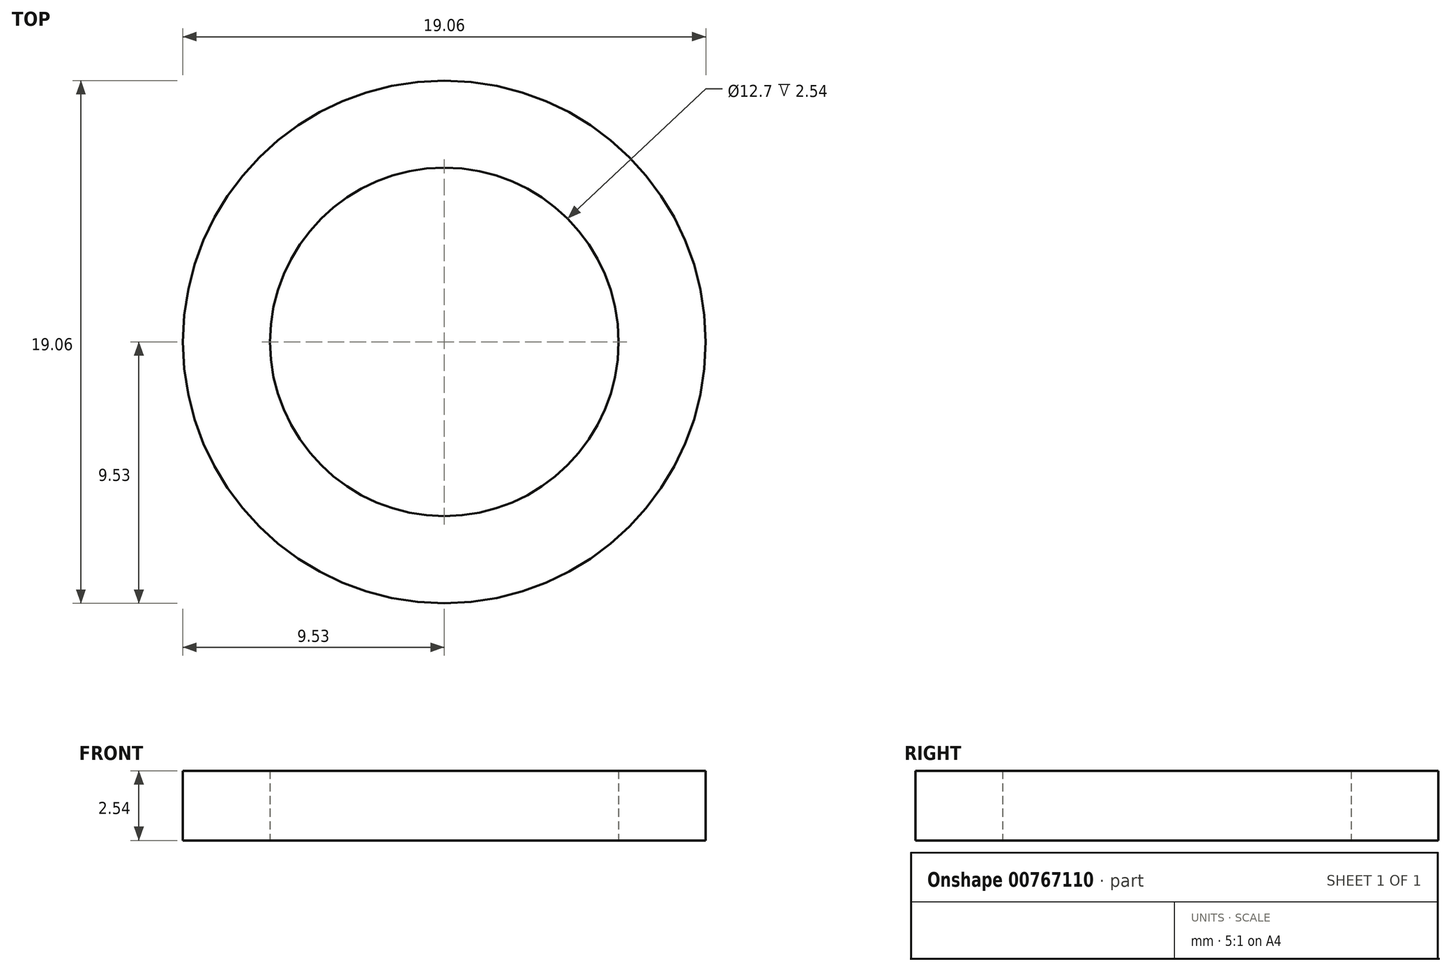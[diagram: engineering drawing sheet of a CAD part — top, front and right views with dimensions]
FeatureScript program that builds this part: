
annotation { "Feature Type Name" : "Feature", "Feature Type Description" : "" }
export const myFeature = defineFeature(function(context is Context, id is Id, definition is map)
    precondition{}
    {
        {
            var Q0;
            Q0=qCreatedBy(makeId("Top.planeOp"),FACE);
            var sketch = newSketch(context, id + "F0", { "sketchPlane" : qUnion([Q0])});
            skCircle(sketch, "E0", {"center": v(0, 0) * mm, "radius": 9.53 * mm});
            skCircle(sketch, "E1", {"center": v(0, 0) * mm, "radius": 6.35 * mm});
            skSolve(sketch);
        }
        {
            var Q0;
            Q0=makeQuery(id+"F0.imprint","IMPRINT",FACE,{"disambiguationData":[TD([[makeQuery(id+"F0.imprint","IMPRINT",EDGE,{"derivedFrom":sQuery(id+"F0.wireOp",EDGE,"E0")}),1.0]])]});
            extrude(context, id + "F1", {"entities" : qUnion([Q0]), "depth" : 2.54 * mm, "offsetDistance" : 25.4 * mm});
        }
    });
